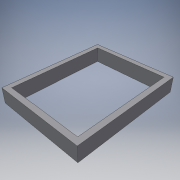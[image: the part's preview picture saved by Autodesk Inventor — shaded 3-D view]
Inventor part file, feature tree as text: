
AUTODESK INVENTOR PART (.ipt)
format: ipt  version: 2016 (Build 200138000, 138)  size: 98,816 bytes
history: native  units: in
note: dims shown in document units (in); Inventor stores cm internally (conversion verified against a paired STEP export)
features: extrude x2, sketch x2
ambient origin geometry x8: Origin, YZ Plane, XZ Plane, XY Plane, X Axis, Y Axis, Z Axis, Center Point
bodies: Solid1 (feature_tree)
feature tree (4):
  extrude  "Extrusion1"  Depth=16.0in
  extrude  "Extrusion2"  Depth=18.0in
  sketch  "Sketch1"  dims[d0=20.0in d1=16.0in]
  sketch  "Sketch2"  dims[d2=2.8in d3=0.0in d4=18.0in d5=14.0in d7=2.8in d8=0.0in]
